# Revit family: 3f_filippi_-_3f_cub_vs_3f_filippi_-_56337_-_3f_cub_led_100w_cr_vs
name_source: partatom
category: Lighting Fixtures
units: mm (PartAtom-declared; Revit-internal decimal feet)

## family parameters
Cut with Voids When Loaded = No
Host = Face
Light Source = No
Part Type = Normal
Room Calculation Point = No
Round Connector Dimension = Use Diameter
Shared = No

## types (1)
- 3F Filippi - 3F Cub VS (1 x LED, 13981 lm, 108 W, 4000 K)
    Apparent Load = 108 VA
    Approval mark = CE
    CIE Flux Codes = 62 89 98 100 100
    Color Rendering = 80
    Color Temperature = 4000 K
    Control Gear = Electronic ballast
    Default Elevation = 1800 mm
    Description = ILLUMINOTECHNICAL
Luminous efficiency 100% (DLOR 100%, ULOR 0%).
Initial luminous flux of the luminaire 13981 lm.
Symmetric wide direct distribution.
Installation Interdistance Transv.D = 1.02 x hu - Long.D = 1.23 x hu.
Tabular UGR (CIE 117 - 4H-8H; S=0.25H; 70/50/20): RUG 22 - 22.6.
Beam angle: 83° - 91°.
Luminous efficacy 129 lm/W.
Lifetime (L90/B10): 30000 h. (tq+25°C)
Lifetime (L85/B10): 50000 h. (tq+25°C)
Lifetime (L80/B20): 80000 h. (tq+25°C)
Lifetime (L70/B20): 100000 h. (tq+25°C)
Lifetime (L70/B10): 50000 h. (tq+45°C)
Sudden decreased luminous flux after 50000 hours: 0% (C0).
Photobiological safety in compliance with IEC/TR 62778: RG0 risk exempt, (IEC 62471).
In compliance with IEC/EN 62722-2-1 - IEC/EN 62717 standards.

SOURCE
4 linear LED modules 25W/840.
Energy efficiency class (UE 2019/2020 - UE 2019/2015): C.
CIE 13.3 Colour rendering index: CRI >80 (R9 <50%).
IES TM-30 Fidelity Index: Rf = 84 Rg = 95.
CCT nominal colour temperature 4000 K.
Colour initial tolerance (MacAdam): SDCM 3.

MECHANICAL
Housing with double casing in pressed aluminium, powder-coated in white epoxy-polyester, hinged opening.
Quick connection in polycarbonate M20x1.5 cable gland for access to the terminal block.
Ecologic anti-aging injected sealing gasket.
Stainless steel clips.
Total flow recuperator in specular aluminium, with superficial titanium-magnesium treatment, non-iridescent.
VS moulded glass, non-combustible, thickness 4 mm, tempered, anti-glare.
Fixing bracket for busbar or suspension in galvanised steel.
Luminaire with limited surface temperature. - D - (EN 60598-2-24)
Dimensions: 680x680 mm, height 187 mm. Weight 10.975 kg.
IP64 protection degree.
Mechanical strength to impacts IK10 (20 joule).
Glow-wire test resistance 960°C.

ELECTRICAL
Halogen Free electronic wiring 230V-50/60Hz, power factor 0.95, THD <25%, constant output current, class I, 2 driver.
Twin-circuit.
Power of the luminaire 108 W.
ENEC - CE.
SAFE FLICKER: PstLM=<1 and SVM=<0.4 (IEC TR 61547-1 and IEC TR 63158), to ensure a more comfortable and safe light.
Luminaire compliant with EN 60598-2-22 for power supply from a centralised emergency system CPSS (Central Power Supply System), not incorporated in the luminaire - high risk areas excluded. The default power and flux are 100% in AC and 100% in DC.
Ambient temperature from -20°C to +45°C.
Temperature class T6 max 85°C.
Quick connection.
Relative humidity UR: <85%.

INSTALLATION
Ceiling / Suspended.
All accessories dedicated to this product are available on the Catalog and on our website www.3F-Filippi.com.

APPLICATIONS
In commercial environments, exhibition and industrial areas, stores, open areas.

WARNING
Fixture not suitable for cold stores with an ambient temperature <0°C and/or relative humidity >85%.
Luminaire designed for disposal/recycling at end-of-life.
Replaceable (LED only) light source by a professional. Replaceable control gear by a professional.
    Height = 187 mm
    Lamp = 1 x LED
    Lamp Light Flux = 13981 lm
    Lamp Power = 108 W
    Lamp count = 1
    Length = 680 mm
    Lifetime = 50000 h
    Luminous efficacy = 129 lm/W
    Manufacturer = 3F Filippi
    ModVariant = No
    Model = 3F Filippi - 56337 - 3F CUB LED 100W CR VS
    Mounting Place = Ceiling
    Mounting Type = Pendant
    Number of Poles = 1
    OnlyDefault = Yes
    Power Factor = 1
    Product Name = 3F Filippi - 3F Cub VS
    Product group = pendant luminaire
    ProductGroupID = 9
    Protection Class = Protection class I
    Protection Degree = IP 64
    RLX_Detail_Level = 1
    RLX_Emergency_Light_Flux = 0 lm
    RLX_Emergency_Type = 0
    RLX_Emergency_Type_DB = No
    RlxData = <blob elided: 45801 chars, md5=4757308b>
    Socket = socket
    Standby Power = 0 W
    System Light Flux = 13981 lm
    System Power = 108 W
    Type Comments = Product without accessories
    Type Image = 3ffilippi_56337.jpg
    URL = http://relux.com
    VarID = ---
    Voltage = 0 V
    Weight = 0.00 kg
    Width = 680 mm

## geometry (parser evidence)
native form markers: Sweep x10
no freeform markers — native parametric forms only
